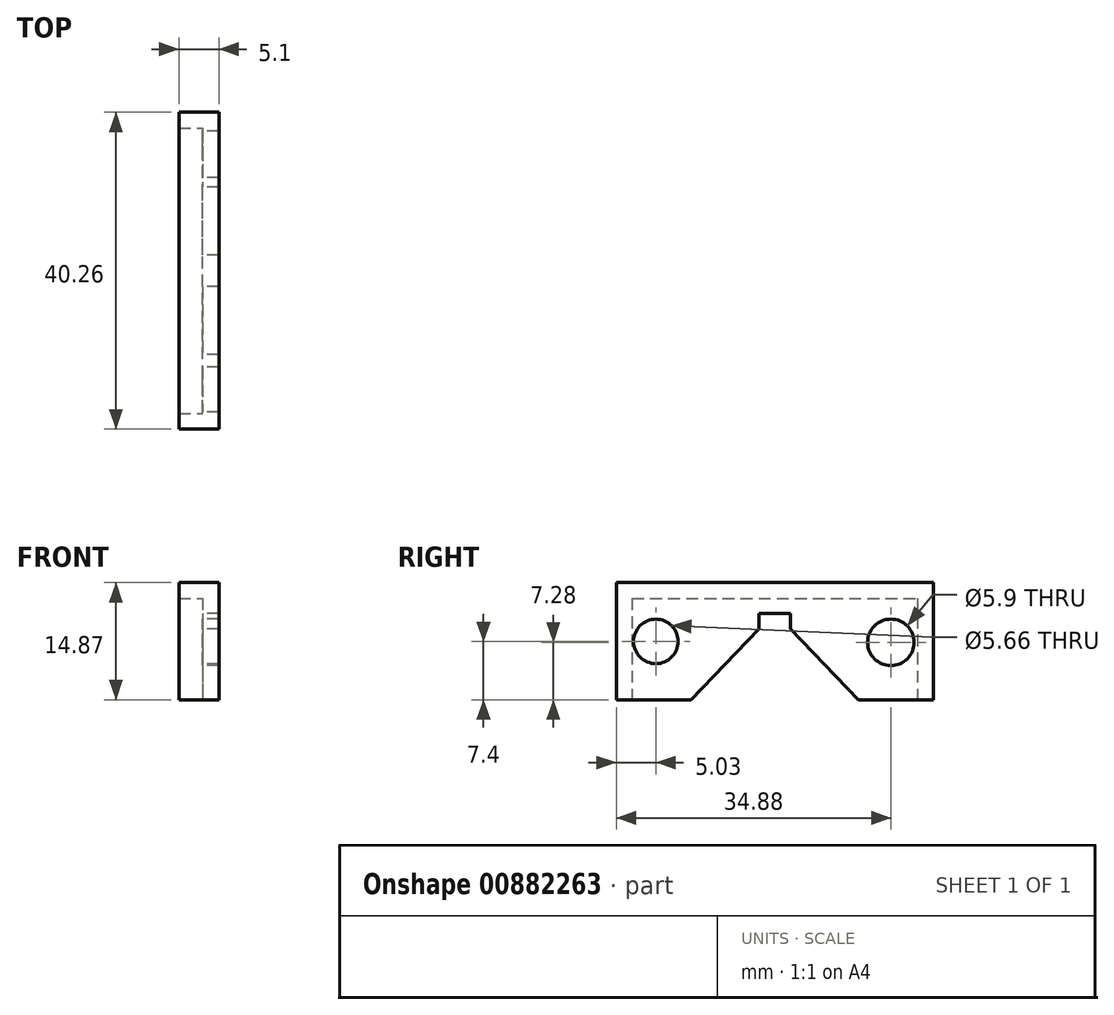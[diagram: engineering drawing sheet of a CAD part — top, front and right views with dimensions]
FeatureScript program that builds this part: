
annotation { "Feature Type Name" : "Feature", "Feature Type Description" : "" }
export const myFeature = defineFeature(function(context is Context, id is Id, definition is map)
    precondition{}
    {
        {
            var Q0;
            Q0=qCreatedBy(makeId("Right.planeOp"),FACE);
            var sketch = newSketch(context, id + "F0", { "sketchPlane" : qUnion([Q0])});
            skLineSegment(sketch, "E0.bottom", {"start": v(-20.13, 14.87) * mm, "end": v(20.13, 14.87) * mm, "construction": true});
            skLineSegment(sketch, "E0.left", {"start": v(-20.13, 14.87) * mm, "end": v(-20.13, 0) * mm});
            skLineSegment(sketch, "E0.right", {"start": v(20.13, 14.87) * mm, "end": v(20.13, 0) * mm});
            skLineSegment(sketch, "E1", {"start": v(17.7, 14.87) * mm, "end": v(17.7, 0) * mm, "construction": true});
            skLineSegment(sketch, "E2", {"start": v(17.7, 7.44) * mm, "end": v(20.13, 7.44) * mm, "construction": true});
            skLineSegment(sketch, "E3", {"start": v(-20.13, 10.23) * mm, "end": v(20.13, 10.23) * mm, "construction": true});
            skLineSegment(sketch, "E4", {"start": v(0, 10.23) * mm, "end": v(0, 14.87) * mm, "construction": true});
            skCircle(sketch, "E5", {"center": v(14.75, 7.28) * mm, "radius": 2.95 * mm});
            skLineSegment(sketch, "E6", {"start": v(-17.93, 10.23) * mm, "end": v(-17.93, 0) * mm, "construction": true});
            skLineSegment(sketch, "E7", {"start": v(-20.13, 5.54) * mm, "end": v(-17.93, 5.54) * mm, "construction": true});
            skCircle(sketch, "E8", {"center": v(-15.1, 7.4) * mm, "radius": 2.83 * mm});
            skLineSegment(sketch, "E9", {"start": v(-2, 10.97) * mm, "end": v(2, 10.97) * mm});
            skLineSegment(sketch, "E10", {"start": v(-20.13, 10.97) * mm, "end": v(20.13, 10.97) * mm, "construction": true});
            skLineSegment(sketch, "E11", {"start": v(20.13, 10.97) * mm, "end": v(0, 10.97) * mm, "construction": true});
            skLineSegment(sketch, "E12", {"start": v(0, 10.97) * mm, "end": v(0, 14.87) * mm, "construction": true});
            skLineSegment(sketch, "E13", {"start": v(-20.13, 0) * mm, "end": v(-10.63, 0) * mm});
            skLineSegment(sketch, "E14", {"start": v(20.13, 0) * mm, "end": v(10.63, 0) * mm});
            skLineSegment(sketch, "E15", {"start": v(2, 8.97) * mm, "end": v(10.63, 0) * mm});
            skLineSegment(sketch, "E16", {"start": v(-2, 8.97) * mm, "end": v(-10.63, 0) * mm});
            skLineSegment(sketch, "E17", {"start": v(-20.13, 14.87) * mm, "end": v(20.13, 14.87) * mm});
            skLineSegment(sketch, "E18", {"start": v(-2, 10.97) * mm, "end": v(-2, 8.97) * mm});
            skLineSegment(sketch, "E19", {"start": v(2, 10.97) * mm, "end": v(2, 8.97) * mm});
            skSolve(sketch);
        }
        {
            var Q0;
            Q0=qCreatedBy(makeId("Right.planeOp"),FACE);
            var sketch = newSketch(context, id + "F1", { "sketchPlane" : qUnion([Q0])});
            skLineSegment(sketch, "E20", {"start": v(20.13, 14.87) * mm, "end": v(-20.13, 14.87) * mm});
            skLineSegment(sketch, "E21", {"start": v(-20.13, 14.87) * mm, "end": v(-20.13, 0) * mm});
            skLineSegment(sketch, "E22", {"start": v(20.13, 0) * mm, "end": v(20.13, 14.87) * mm});
            skLineSegment(sketch, "E23.0", {"start": v(-18.13, 12.87) * mm, "end": v(-18.13, 0) * mm});
            skLineSegment(sketch, "E23.1", {"start": v(-18.13, 12.87) * mm, "end": v(18.13, 12.87) * mm});
            skLineSegment(sketch, "E23.2", {"start": v(18.13, 12.87) * mm, "end": v(18.13, 0) * mm});
            skLineSegment(sketch, "E24", {"start": v(-20.13, 0) * mm, "end": v(-18.13, 0) * mm});
            skLineSegment(sketch, "E25", {"start": v(20.13, 0) * mm, "end": v(18.13, 0) * mm});
            skSolve(sketch);
        }
        {
            var Q0;
            Q0 = qSketchRegion(id + "F0", true);
            extrude(context, id + "F2", {"entities" : qUnion([Q0]), "depth" : 2.1 * mm, "offsetDistance" : 25 * mm});
        }
        {
            var Q0;
            Q0=makeQuery(id+"F1.imprint","IMPRINT",FACE,{"disambiguationData":[TD([[makeQuery(id+"F1.imprint","IMPRINT",EDGE,{"derivedFrom":sQuery(id+"F1.wireOp",EDGE,"E20")}),1.0]])]});
            extrude(context, id + "F3", {"entities" : qUnion([Q0]), "operationType" : NewBodyOperationType.ADD, "oppositeDirection" : true, "depth" : 3 * mm, "offsetDistance" : 25 * mm});
        }
    });
